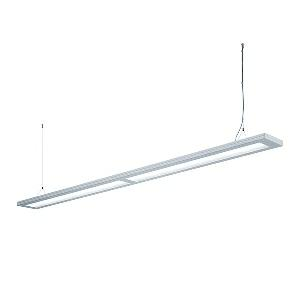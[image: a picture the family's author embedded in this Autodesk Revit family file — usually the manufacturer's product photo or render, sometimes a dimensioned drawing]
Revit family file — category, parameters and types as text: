
# Revit family: lavigo_-_dpp_24000_840_d_g2_00750566_2205
name_source: partatom
category: Lighting Fixtures
units: mm (PartAtom-declared; Revit-internal decimal feet)

## family parameters
Cut with Voids When Loaded = No
Host = Face
Light Source = No
Part Type = Normal
Room Calculation Point = No
Round Connector Dimension = Use Diameter
Shared = No

## types (1)
- LAVIGO - DPP 24000/840/D/G2 (1 x LED, 24000 lm, 4000K)
    Apparent Load = 158 VA
    Approval mark = CE
    CIE Flux Codes = 60 87 97 14 100
    Color Rendering = 80-89
    Color Temperature = 4000K
    Control Gear = Electronic ballast
    Default Elevation = 1800 mm
    Description = DPP 24000/840/D/G2|Suspended luminaire|light source: LED|connected load: 220-240 V, 50/60 Hz|Power consumption: approx. 158 W|standby: approx. 0,50|luminous flux: 24000 lm|luminous efficacy: 151 lm/W|light distribution: Direct/indirect|direct ratio: approx. 14 %|colour temperature: Cold white, ca. 4000 K|color rendering index (CRI): >= 80|chromaticity tolerance:  3 SDCM|System of protection: IP 20|technology: Continuously dimmable|luminaire body|material: Steel/plastic|surface: Powder coatet|colour: Silver metallic|lamp cover: Polycarbonate (PC), Clear|mains lead: 1.00 m With free stranded wires|Fastening: Steel cable 0.3 - 0.7 m|decorative contrast side parts: Flint grey|glare control: Prism aperture|luminance(L65): <= 2700 cd/m|unified glare rating(4H 8H): <=  16|special features: Canopy colour (pure white), Cradle to Cradle Certified TM, DALI - dimming via digital rotary dimmer, DALI Load 3x, Direct light component with edge light and light-guide technology for homogenous light exit, Integration into DALI light management systems, Flicker-free, TouchDIM - dimming via standard switch|
    Frequency = 50 Hz
    Height = 36 mm
    Lamp = 1 x LED
    Lamp Light Flux = 24000 lm
    Lamp count = 1
    Length = 2430 mm
    Luminous efficacy = 152 lm/W
    Manufacturer = Waldmann
    ModVariant = No
    Model = 00750566
    Mounting Place = Ceiling
    Mounting Type = Pendant
    Number of Poles = 1
    OnlyDefault = Yes
    Power Factor = 1
    Product Name = LAVIGO - DPP 24000/840/D/G2
    Product group = Suspended luminaire
    ProductGroupID = 9
    Protection Class = Protection class I
    Protection Degree = IP 20
    RLX_Detail_Level = 1
    RLX_Emergency_Light_Flux = 0 lm
    RLX_Emergency_Type = 0
    RLX_Emergency_Type_DB = No
    RlxData = <blob elided: 26253 chars, md5=4c6de73d>
    Socket = socket
    Standby Power = 0 W
    System Light Flux = 24000 lm
    System Power = 158 W
    Type Comments = Product without accessories
    Type Image = 121742000-00681441.jpg
    URL = http://relux.com
    VarID = ---
    Voltage = 230 V
    Voltage Range = 220-240 V
    Weight = 0.00 kg
    Width = 200 mm  [stored 0.656168 ft]

note: [stored X ft] marks values corroborated as IEEE doubles in the binary element streams (Revit-internal decimal feet)

## geometry (parser evidence)
native form markers: Blend x4, Sweep x13
no freeform markers — native parametric forms only
